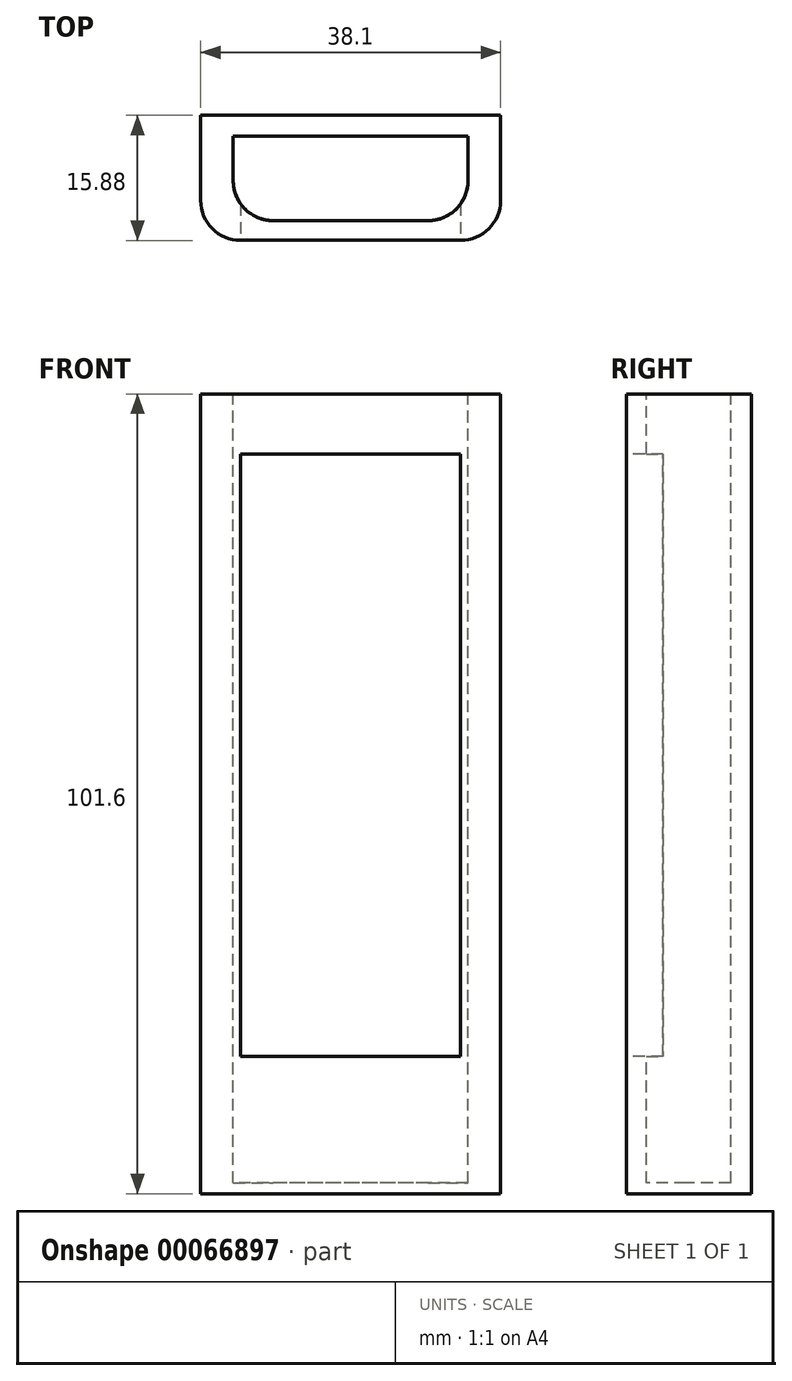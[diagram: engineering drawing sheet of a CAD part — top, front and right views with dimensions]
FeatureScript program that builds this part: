
annotation { "Feature Type Name" : "Feature", "Feature Type Description" : "" }
export const myFeature = defineFeature(function(context is Context, id is Id, definition is map)
    precondition{}
    {
        {
            var Q0;
            Q0=qCreatedBy(makeId("Front.planeOp"),FACE);
            var sketch = newSketch(context, id + "F0", { "sketchPlane" : qUnion([Q0])});
            skLineSegment(sketch, "E0.bottom", {"start": v(-48.8, 18.07) * mm, "end": v(-10.7, 18.07) * mm});
            skLineSegment(sketch, "E0.top", {"start": v(-48.8, -83.53) * mm, "end": v(-10.7, -83.53) * mm});
            skLineSegment(sketch, "E0.left", {"start": v(-48.8, 18.07) * mm, "end": v(-48.8, -83.53) * mm});
            skLineSegment(sketch, "E0.right", {"start": v(-10.7, 18.07) * mm, "end": v(-10.7, -83.53) * mm});
            skSolve(sketch);
        }
        {
            var Q0;
            Q0=makeQuery(id+"F0.imprint","IMPRINT",FACE,{"disambiguationData":[TD([[makeQuery(id+"F0.imprint","IMPRINT",EDGE,{"derivedFrom":sQuery(id+"F0.wireOp",EDGE,"E0.bottom")}),-1.0]])]});
            extrude(context, id + "F1", {"entities" : qUnion([Q0]), "depth" : 15.88 * mm});
        }
        {
            var Q0;
            Q0=makeQuery(id+"F1.opExtrude","CAP_FACE",FACE,{"disambiguationData":[OSD([sQuery(id+"F0.wireOp",EDGE,"E0.bottom"),sQuery(id+"F0.wireOp",EDGE,"E0.top"),sQuery(id+"F0.wireOp",EDGE,"E0.left"),sQuery(id+"F0.wireOp",EDGE,"E0.right")])],"isStart":false});
            var sketch = newSketch(context, id + "F2", { "sketchPlane" : qUnion([Q0])});
            skLineSegment(sketch, "E1.bottom", {"start": v(-43.72, 10.45) * mm, "end": v(-15.78, 10.45) * mm});
            skLineSegment(sketch, "E1.top", {"start": v(-43.72, -66.07) * mm, "end": v(-15.78, -66.07) * mm});
            skLineSegment(sketch, "E1.left", {"start": v(-43.72, 10.45) * mm, "end": v(-43.72, -66.07) * mm});
            skLineSegment(sketch, "E1.right", {"start": v(-15.78, 10.45) * mm, "end": v(-15.78, -66.07) * mm});
            skSolve(sketch);
        }
        {
            var Q0;
            Q0=makeQuery(id+"F2.imprint","IMPRINT",FACE,{"disambiguationData":[TD([[makeQuery(id+"F2.imprint","IMPRINT",EDGE,{"derivedFrom":sQuery(id+"F2.wireOp",EDGE,"E1.bottom")}),-1.0]])]});
            extrude(context, id + "F3", {"entities" : qUnion([Q0]), "operationType" : NewBodyOperationType.REMOVE, "oppositeDirection" : true, "depth" : 12.7 * mm});
        }
        {
            var Q0;
            Q0=makeQuery(id+"F1.opExtrude","SWEPT_FACE",FACE,{"disambiguationData":[OSD([sQuery(id+"F0.wireOp",EDGE,"E0.bottom")])]});
            var sketch = newSketch(context, id + "F4", { "sketchPlane" : qUnion([Q0])});
            skLineSegment(sketch, "E2.bottom", {"start": v(-14.84, -2.63) * mm, "end": v(-44.66, -2.63) * mm});
            skLineSegment(sketch, "E2.top", {"start": v(-14.84, -13.38) * mm, "end": v(-44.66, -13.38) * mm});
            skLineSegment(sketch, "E2.left", {"start": v(-14.84, -2.63) * mm, "end": v(-14.84, -13.38) * mm});
            skLineSegment(sketch, "E2.right", {"start": v(-44.66, -2.63) * mm, "end": v(-44.66, -13.38) * mm});
            skSolve(sketch);
        }
        {
            var Q0;
            Q0=makeQuery(id+"F4.imprint","IMPRINT",FACE,{"disambiguationData":[TD([[makeQuery(id+"F4.imprint","IMPRINT",EDGE,{"derivedFrom":sQuery(id+"F4.wireOp",EDGE,"E2.bottom")}),1.0]])]});
            extrude(context, id + "F5", {"entities" : qUnion([Q0]), "operationType" : NewBodyOperationType.REMOVE, "oppositeDirection" : true, "depth" : 100.23 * mm});
        }
        {
            var Q0;
            Q0=makeQuery(id+"F1.opExtrude","CAP_EDGE",EDGE,{"disambiguationData":[OSD([sQuery(id+"F0.wireOp",EDGE,"E0.right")])],"isStart":false});
            var Q1;
            Q1=makeQuery(id+"F1.opExtrude","CAP_EDGE",EDGE,{"disambiguationData":[OSD([sQuery(id+"F0.wireOp",EDGE,"E0.left")])],"isStart":false});
            var Q2;
            Q2=makeQuery(id+"F5.boolean.opBoolean","COPY",EDGE,{"derivedFrom":makeQuery(id+"F5.opExtrude","SWEPT_EDGE",EDGE,{"disambiguationData":[OSD([sQuery(id+"F4.wireOp",EDGE,"E2.top"),sQuery(id+"F4.wireOp",EDGE,"E2.left")])]})});
            var Q3;
            Q3=makeQuery(id+"F5.boolean.opBoolean","COPY",EDGE,{"derivedFrom":makeQuery(id+"F5.opExtrude","SWEPT_EDGE",EDGE,{"disambiguationData":[OSD([sQuery(id+"F4.wireOp",EDGE,"E2.top"),sQuery(id+"F4.wireOp",EDGE,"E2.right")])]})});
            fillet(context, id + "F6", {"entities" : qUnion([Q0, Q1, Q2, Q3]), "radius" : 5.08 * mm, "tangentPropagation" : true, "allowEdgeOverflow" : false});
        }
    });
